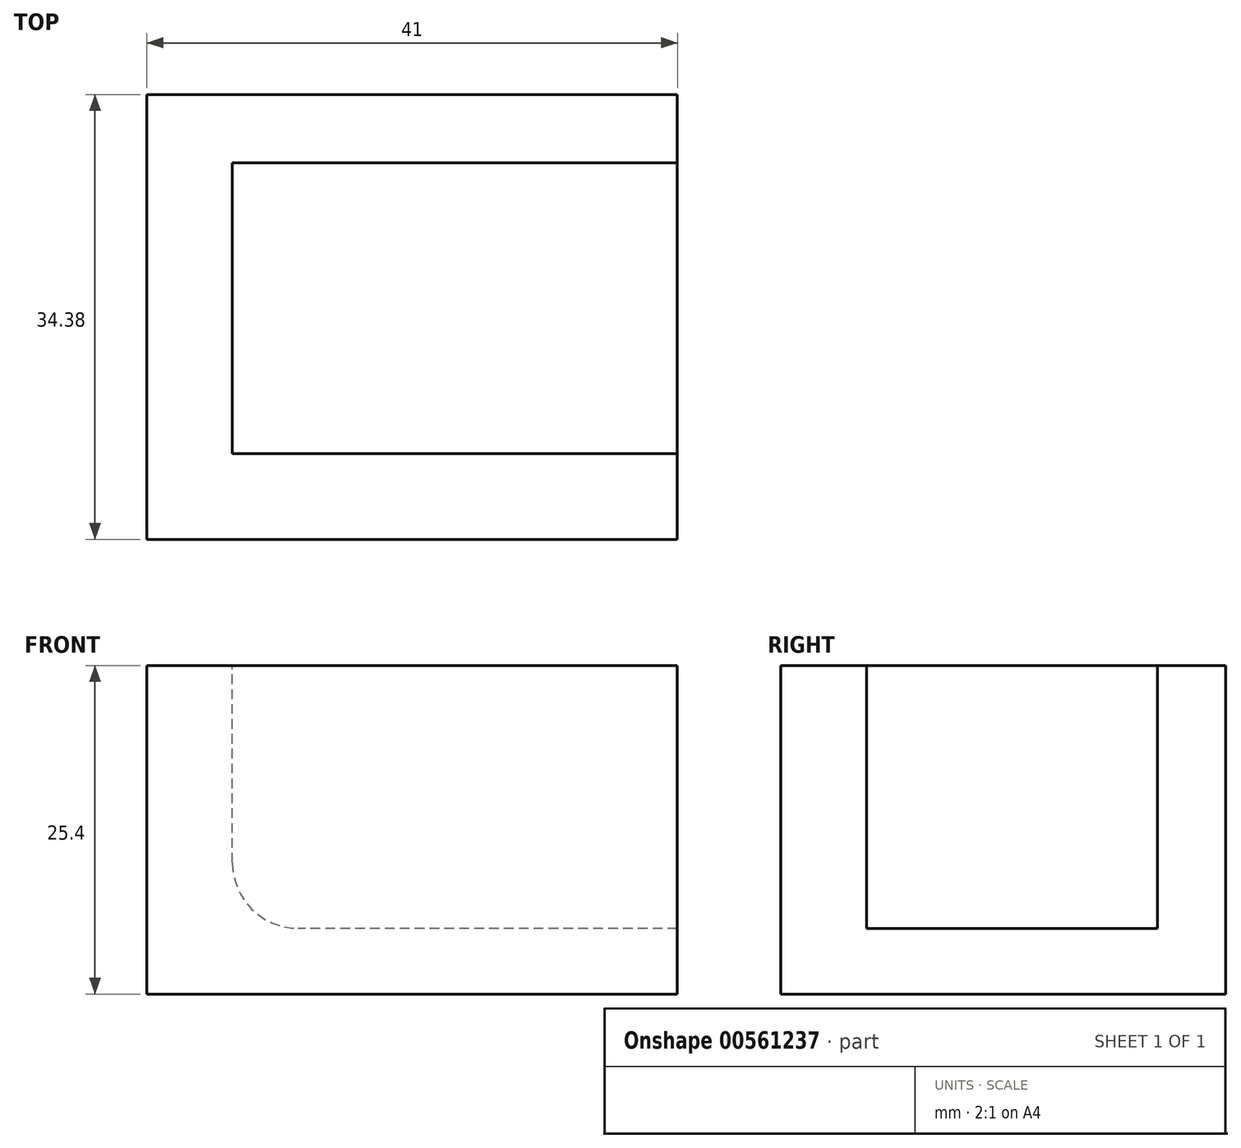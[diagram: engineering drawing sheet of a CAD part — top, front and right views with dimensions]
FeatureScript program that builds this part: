
annotation { "Feature Type Name" : "Feature", "Feature Type Description" : "" }
export const myFeature = defineFeature(function(context is Context, id is Id, definition is map)
    precondition{}
    {
        {
            var Q0;
            Q0=qCreatedBy(makeId("Top.planeOp"),FACE);
            var sketch = newSketch(context, id + "F0", { "sketchPlane" : qUnion([Q0])});
            skLineSegment(sketch, "E0.bottom", {"start": v(0, 0) * mm, "end": v(41, 0) * mm});
            skLineSegment(sketch, "E0.top", {"start": v(0, 34.38) * mm, "end": v(41, 34.38) * mm});
            skLineSegment(sketch, "E0.left", {"start": v(0, 0) * mm, "end": v(0, 34.38) * mm});
            skLineSegment(sketch, "E0.right", {"start": v(41, 0) * mm, "end": v(41, 34.38) * mm});
            skSolve(sketch);
        }
        {
            var Q0;
            Q0=makeQuery(id+"F0.imprint","IMPRINT",FACE,{"disambiguationData":[TD([[makeQuery(id+"F0.imprint","IMPRINT",EDGE,{"derivedFrom":sQuery(id+"F0.wireOp",EDGE,"E0.bottom")}),1.0]])]});
            extrude(context, id + "F1", {"entities" : qUnion([Q0]), "depth" : 25.4 * mm, "offsetDistance" : 25.4 * mm});
        }
        {
            var Q0;
            Q0=makeQuery(id+"F1.opExtrude","CAP_FACE",FACE,{"disambiguationData":[OSD([sQuery(id+"F0.wireOp",EDGE,"E0.bottom"),sQuery(id+"F0.wireOp",EDGE,"E0.top"),sQuery(id+"F0.wireOp",EDGE,"E0.left"),sQuery(id+"F0.wireOp",EDGE,"E0.right")])],"isStart":false});
            var sketch = newSketch(context, id + "F2", { "sketchPlane" : qUnion([Q0])});
            skLineSegment(sketch, "E1.bottom", {"start": v(41, 29.1) * mm, "end": v(6.61, 29.1) * mm});
            skLineSegment(sketch, "E1.top", {"start": v(41, 6.61) * mm, "end": v(6.61, 6.61) * mm});
            skLineSegment(sketch, "E1.left", {"start": v(41, 29.1) * mm, "end": v(41, 6.61) * mm});
            skLineSegment(sketch, "E1.right", {"start": v(6.61, 29.1) * mm, "end": v(6.61, 6.61) * mm});
            skSolve(sketch);
        }
        {
            var Q0;
            Q0=makeQuery(id+"F2.imprint","IMPRINT",FACE,{"disambiguationData":[TD([[makeQuery(id+"F2.imprint","IMPRINT",EDGE,{"derivedFrom":sQuery(id+"F2.wireOp",EDGE,"E1.bottom")}),1.0]])]});
            extrude(context, id + "F3", {"entities" : qUnion([Q0]), "operationType" : NewBodyOperationType.REMOVE, "oppositeDirection" : true, "depth" : 20.32 * mm, "offsetDistance" : 25.4 * mm});
        }
        {
            var Q0;
            Q0=makeQuery(id+"F3.boolean.opBoolean","COPY",EDGE,{"derivedFrom":makeQuery(id+"F3.opExtrude","CAP_EDGE",EDGE,{"disambiguationData":[OSD([sQuery(id+"F2.wireOp",EDGE,"E1.right")])],"isStart":false})});
            fillet(context, id + "F4", {"entities" : qUnion([Q0]), "radius" : 5.08 * mm, "tangentPropagation" : true, "allowEdgeOverflow" : false});
        }
    });
